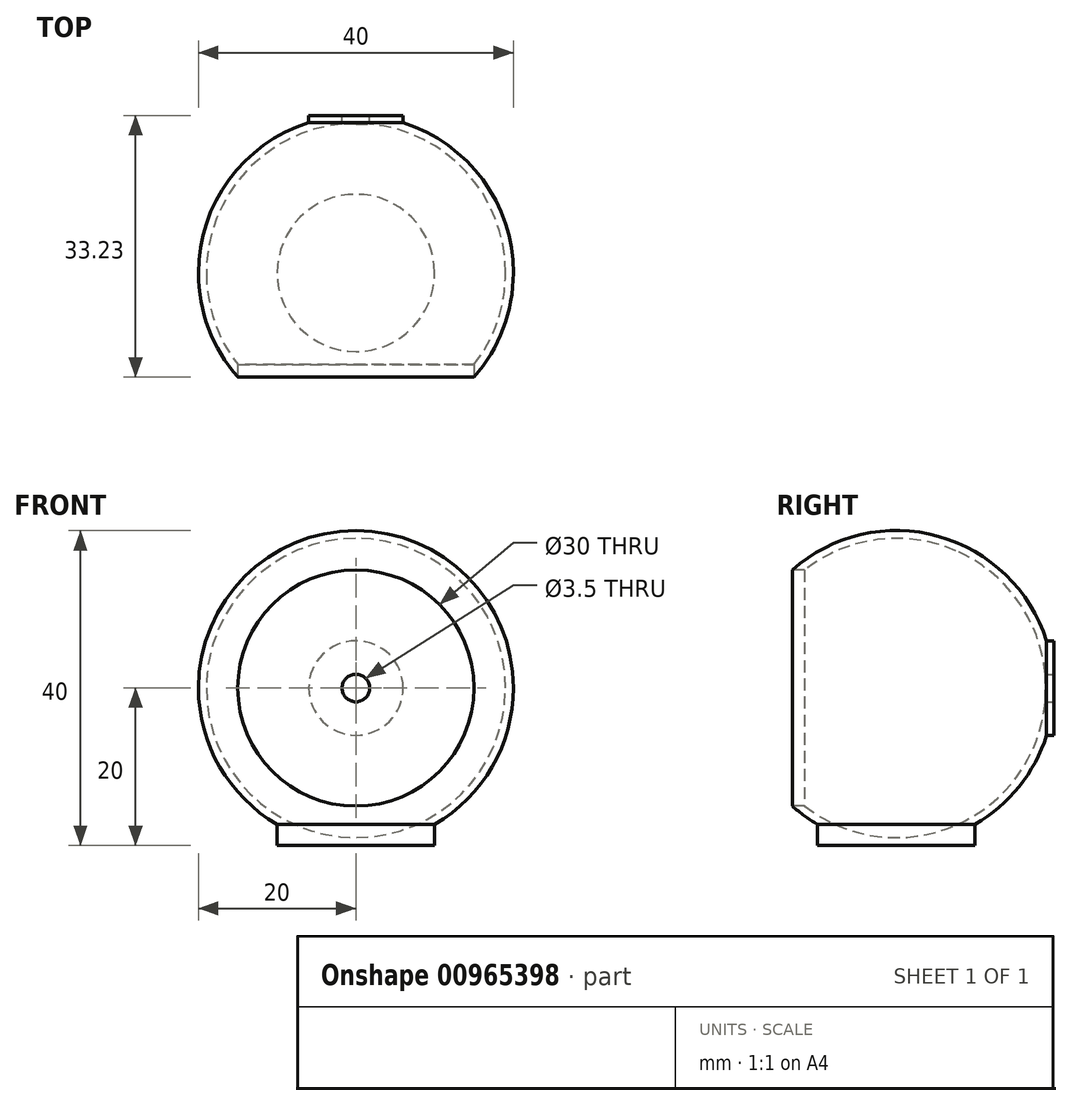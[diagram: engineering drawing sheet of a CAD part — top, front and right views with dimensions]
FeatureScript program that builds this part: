
annotation { "Feature Type Name" : "Feature", "Feature Type Description" : "" }
export const myFeature = defineFeature(function(context is Context, id is Id, definition is map)
    precondition{}
    {
        {
            var Q0;
            Q0=qCreatedBy(makeId("Top.planeOp"),FACE);
            var sketch = newSketch(context, id + "F0", { "sketchPlane" : qUnion([Q0])});
            skLineSegment(sketch, "E0", {"start": v(0, 0) * mm, "end": v(-20, 0) * mm});
            skLineSegment(sketch, "E1", {"start": v(0, 0) * mm, "end": v(20, 0) * mm});
            skPoint(sketch, "E1.endSnap0", {"position": v(-10, 0) * mm});
            skArc(sketch, "E2", {"start": v(20, 0) * mm, "mid": v(0, 20) * mm, "end": v(-20, 0) * mm});
            skArc(sketch, "E3.0", {"start": v(19, 0) * mm, "mid": v(0, 19) * mm, "end": v(-19, 0) * mm});
            skSolve(sketch);
        }
        {
            var Q0;
            {var subQ0=sQuery(id+"F0.wireOp",EDGE,"E2");Q0=makeQuery(id+"F0.imprint","IMPRINT",FACE,{"disambiguationData":[TD([[makeQuery(id+"F0.imprint","IMPRINT",EDGE,{"derivedFrom":subQ0}),1.0]])]});}
            var Q1;
            Q1=sQuery(id+"F0.wireOp",EDGE,"E1");
            revolve(context, id + "F1", {"surfaceOperationType" : NewSurfaceOperationType.NEW, "entities" : qUnion([Q0]), "axis" : qUnion([Q1]), "revolveType" : RevolveType.FULL});
        }
        {
            var Q0;
            Q0=qCreatedBy(makeId("Front.planeOp"),FACE);
            cPlane(context, id + "F2", {"entities" : qUnion([Q0]), "cplaneType" : CPlaneType.OFFSET, "offset" : 20 * mm, "width" : 150 * mm, "height" : 150 * mm});
        }
        {
            var Q0;
            Q0=qCreatedBy(id+"F2.planeOp",FACE);
            var sketch = newSketch(context, id + "F3", { "sketchPlane" : qUnion([Q0])});
            skCircle(sketch, "E4", {"center": v(0, 0) * mm, "radius": 15 * mm});
            skSolve(sketch);
        }
        {
            var Q0;
            Q0=makeQuery(id+"F3.imprint","IMPRINT",FACE,{"disambiguationData":[TD([[makeQuery(id+"F3.imprint","IMPRINT",EDGE,{"derivedFrom":sQuery(id+"F3.wireOp",EDGE,"E4")}),1.0]])]});
            extrude(context, id + "F4", {"entities" : qUnion([Q0]), "operationType" : NewBodyOperationType.REMOVE, "oppositeDirection" : true, "depth" : 25 * mm, "offsetDistance" : 25 * mm});
        }
        {
            var Q0;
            Q0=qCreatedBy(makeId("Front.planeOp"),FACE);
            cPlane(context, id + "F5", {"entities" : qUnion([Q0]), "cplaneType" : CPlaneType.OFFSET, "offset" : 20 * mm, "oppositeDirection" : true, "width" : 150 * mm, "height" : 150 * mm});
        }
        {
            var Q0;
            Q0=qCreatedBy(id+"F5.planeOp",FACE);
            var sketch = newSketch(context, id + "F6", { "sketchPlane" : qUnion([Q0])});
            skCircle(sketch, "E5", {"center": v(0, 0) * mm, "radius": 6 * mm});
            skSolve(sketch);
        }
        {
            var Q0;
            Q0=makeQuery(id+"F6.imprint","IMPRINT",FACE,{"disambiguationData":[TD([[makeQuery(id+"F6.imprint","IMPRINT",EDGE,{"derivedFrom":sQuery(id+"F6.wireOp",EDGE,"E5")}),1.0]])]});
            extrude(context, id + "F7", {"entities" : qUnion([Q0]), "operationType" : NewBodyOperationType.ADD, "endBound" : BoundingType.UP_TO_NEXT, "depth" : 25 * mm, "offsetDistance" : 25 * mm});
        }
        {
            var Q0;
            Q0=makeQuery(id+"F7.opExtrude","CAP_FACE",FACE,{"disambiguationData":[OSD([sQuery(id+"F6.wireOp",EDGE,"E5")])],"isStart":true});
            var sketch = newSketch(context, id + "F8", { "sketchPlane" : qUnion([Q0])});
            skCircle(sketch, "E6", {"center": v(0, 0) * mm, "radius": 1.75 * mm});
            skSolve(sketch);
        }
        {
            var Q0;
            Q0=makeQuery(id+"F8.imprint","IMPRINT",FACE,{"disambiguationData":[TD([[makeQuery(id+"F8.imprint","IMPRINT",EDGE,{"derivedFrom":sQuery(id+"F8.wireOp",EDGE,"E6")}),1.0]])]});
            extrude(context, id + "F9", {"entities" : qUnion([Q0]), "operationType" : NewBodyOperationType.REMOVE, "endBound" : BoundingType.UP_TO_NEXT, "oppositeDirection" : true, "depth" : 25 * mm, "offsetDistance" : 25 * mm});
        }
        {
            var Q0;
            Q0=qCreatedBy(makeId("Top.planeOp"),FACE);
            cPlane(context, id + "F10", {"entities" : qUnion([Q0]), "cplaneType" : CPlaneType.OFFSET, "offset" : 20 * mm, "oppositeDirection" : true, "width" : 150 * mm, "height" : 150 * mm});
        }
        {
            var Q0;
            Q0=qCreatedBy(id+"F10.planeOp",FACE);
            var sketch = newSketch(context, id + "F11", { "sketchPlane" : qUnion([Q0])});
            skCircle(sketch, "E7", {"center": v(0, 0) * mm, "radius": 10 * mm});
            skSolve(sketch);
        }
        {
            var Q0;
            Q0=makeQuery(id+"F11.imprint","IMPRINT",FACE,{"disambiguationData":[TD([[makeQuery(id+"F11.imprint","IMPRINT",EDGE,{"derivedFrom":sQuery(id+"F11.wireOp",EDGE,"E7")}),1.0]])]});
            extrude(context, id + "F12", {"entities" : qUnion([Q0]), "operationType" : NewBodyOperationType.ADD, "endBound" : BoundingType.UP_TO_NEXT, "depth" : 25 * mm, "offsetDistance" : 25 * mm});
        }
    });
